# Revit family: AFPD
name_source: partatom
category: Mechanical Equipment
revit_build: Autodesk Revit 2015 (Build: 20140606_1530(x64)
units: mm (PartAtom-declared; Revit-internal decimal feet)

## types (16) — shared parameters
Description = Angle Face Plenum Diffuser
Manufacturer = United Enertech Corporation
Model = AFPD
Type Comments = Consult Factory for Max. Sizes
URL = https://unitedenertech.com

## per-type parameters (varying)
| type | F | Grille Height | Grille Length | Height | T |
| AFPD-1408-5 (2000 cfm) | 0' - 10" | 0' - 8" | 1' - 2" | 1' - 2" | 1' - 4" |
| AFPD-1608-6 (2400 cfm) | 0' - 10" | 0' - 8" | 1' - 4" | 1' - 2" | 1' - 6" |
| AFPD-2008-7.5 (3000 cfm) | 0' - 10" | 0' - 8" | 1' - 8" | 1' - 2" | 1' - 10" |
| AFPD-2010-8.5 (3400 cfm) | 1' - 0" | 0' - 10" | 1' - 8" | 1' - 5" | 1' - 10" |
| AFPD-2210-10 (4000 cfm) | 1' - 0" | 0' - 10" | 1' - 10" | 1' - 5" | 2' - 0" |
| AFPD-2410-12.5 (5000 cfm) | 1' - 0" | 0' - 10" | 2' - 0" | 1' - 5" | 2' - 2" |
| AFPD-2810-15 (6000 cfm) | 1' - 0" | 0' - 10" | 2' - 4" | 1' - 5" | 2' - 6" |
| AFPD-3016-20 (8000 cfm) | 1' - 6" | 1' - 4" | 2' - 6" | 2' - 2" | 2' - 8" |
| AFPD-3616-25 (10000 cfm) | 1' - 6" | 1' - 4" | 3' - 0" | 2' - 2" | 2' - 4" |
| AFPD-3618-30 (12000 cfm) | 1' - 8" | 1' - 6" | 3' - 0" | 2' - 4" | 3' - 2" |
| AFPD-3820-40 (16000 cfm) | 1' - 10" | 1' - 8" | 3' - 2" | 2' - 8" | 3' - 4" |
| AFPD-4222-50 (20000 cfm) | 2' - 0" | 1' - 10" | 3' - 6" | 2' - 10" | 3' - 8" |
| AFPD-4624-62.5 (25000 cfm) | 2' - 2" | 2' - 0" | 3' - 10" | 3' - 0" | 4' - 0" |
| AFPD-7216-80 (32000 cfm) | 1' - 6" | 1' - 4" | 6' - 0" | 2' - 2" | 6' - 2" |
| AFPD-7220-100 (40000 cfm) | 1' - 10" | 1' - 8" | 6' - 0" | 2' - 7" | 6' - 2" |
| AFPD-7224-120 (48000 cfm) | 2' - 2" | 2' - 0" | 6' - 0" | 3' - 0" | 6' - 2" |

## geometry (parser evidence)
native form markers: Sweep x8
no freeform markers — native parametric forms only
